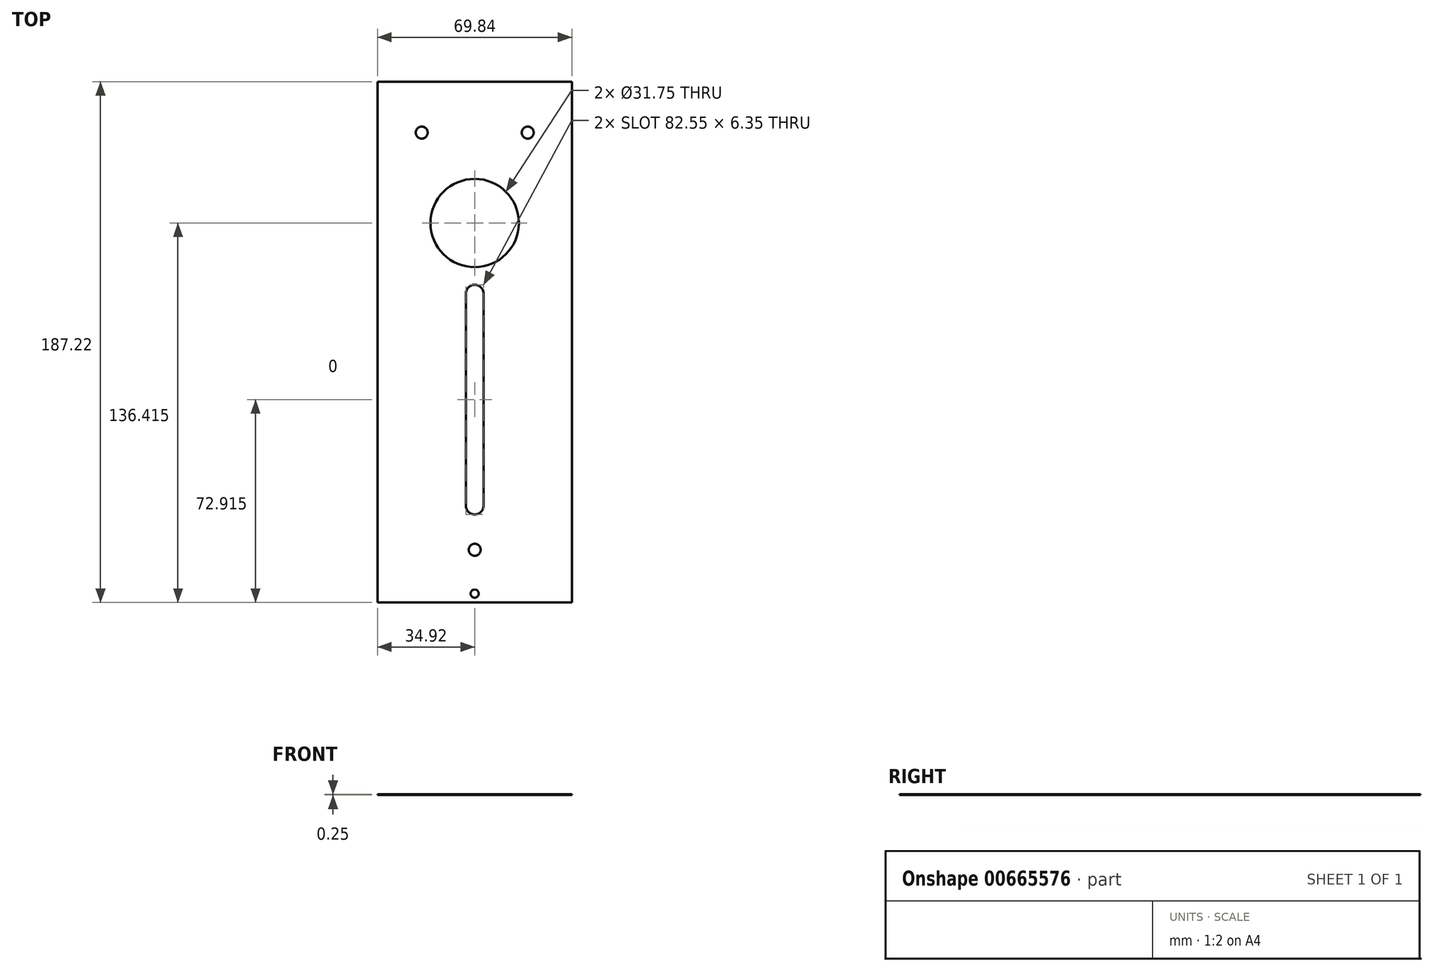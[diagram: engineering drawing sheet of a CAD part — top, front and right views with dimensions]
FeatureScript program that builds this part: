
annotation { "Feature Type Name" : "Feature", "Feature Type Description" : "" }
export const myFeature = defineFeature(function(context is Context, id is Id, definition is map)
    precondition{}
    {
        {
            assignVariable(context, id + "F0", {"name" : "baseThickness", "anyValue" : 0.25});
        }
        {
            var Q0;
            Q0=qCreatedBy(makeId("Top.planeOp"),FACE);
            var sketch = newSketch(context, id + "F1", { "sketchPlane" : qUnion([Q0])});
            skLineSegment(sketch, "E0.bottom", {"start": v(-34.92, 93.6) * mm, "end": v(34.92, 93.6) * mm});
            skLineSegment(sketch, "E0.top", {"start": v(-34.92, -93.6) * mm, "end": v(34.92, -93.6) * mm});
            skLineSegment(sketch, "E0.left", {"start": v(-34.92, 93.6) * mm, "end": v(-34.92, -93.6) * mm});
            skLineSegment(sketch, "E0.right", {"start": v(34.93, 93.6) * mm, "end": v(34.93, -93.6) * mm});
            skCircle(sketch, "E1", {"center": v(0, 42.8) * mm, "radius": 15.88 * mm});
            skCircle(sketch, "E2", {"center": v(-19.05, 75.32) * mm, "radius": 2.15 * mm});
            skCircle(sketch, "E3", {"center": v(19.05, 75.32) * mm, "radius": 2.15 * mm});
            skArc(sketch, "E4", {"start": v(3.17, 17.4) * mm, "mid": v(0, 20.58) * mm, "end": v(-3.17, 17.4) * mm});
            skArc(sketch, "E5", {"start": v(-3.18, -58.8) * mm, "mid": v(0, -61.97) * mm, "end": v(3.18, -58.8) * mm});
            skLineSegment(sketch, "E6", {"start": v(-3.18, 17.4) * mm, "end": v(-3.18, -58.8) * mm});
            skLineSegment(sketch, "E7", {"start": v(3.17, -58.8) * mm, "end": v(3.17, 17.4) * mm});
            skCircle(sketch, "E8", {"center": v(0, -74.67) * mm, "radius": 2.15 * mm});
            skCircle(sketch, "E9", {"center": v(0, -90.43) * mm, "radius": 1.47 * mm});
            skSolve(sketch);
        }
        {
            var Q0;
            Q0=makeQuery(id+"F1.imprint","IMPRINT",FACE,{"disambiguationData":[TD([[makeQuery(id+"F1.imprint","IMPRINT",EDGE,{"derivedFrom":sQuery(id+"F1.wireOp",EDGE,"E0.bottom")}),-1.0]])]});
            extrude(context, id + "F2", {"entities" : qUnion([Q0]), "depth" : (getVariable(context, 'baseThickness')) * mm, "offsetDistance" : 25.4 * mm});
        }
    });
